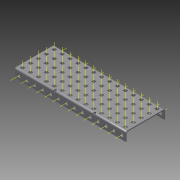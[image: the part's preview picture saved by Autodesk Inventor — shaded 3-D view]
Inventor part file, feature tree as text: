
AUTODESK INVENTOR PART (.ipt)
format: ipt  version: 2015 (Build 190159000, 159)  size: 2,581,504 bytes
history: native  units: in
note: dims shown in document units (in); Inventor stores cm internally (conversion verified against a paired STEP export)
features: other x104, pattern_linear x2, sheet_metal_op x1, extrude x1, imported_body x1, sketch x1
ambient origin geometry x8: Origin, YZ Plane, XZ Plane, XY Plane, X Axis, Y Axis, Z Axis, Center Point
bodies: Body1 (feature_tree)
feature tree (110):
  sheet_metal_op  "Fold1"
  other  "C-Channel"
  extrude  "length cut"  Depth=0.5in
  other  "top axis"
  other  "front axis"
  other  "back axis"
  pattern_linear  "top axes"  Spacing1=0.5in  [1 undecoded]
  pattern_linear  "horiz axes"  Spacing1=0.0in  [1 undecoded]
  other  "right plane"
  imported_body  "Base1"
  sketch  "Sketch1"  dims[d1=0.0in d4=0.5in d5=1.9685in d7=0.5in d10=0.5in d11=0.0in d12=0.0in d13=0.0in d14=-7.0in d15=0.0in d16=0.0in]
  other  "Work Point1"
  other  "Work Axis6"
  other  "Work Axis11"
  other  "Work Axis16"
  other  "Work Axis21"
  other  "Work Point2"
  other  "Work Point3"
  other  "Work Axis36"
  other  "Work Axis37"
  other  "Work Axis38"
  other  "Work Axis39"
  other  "Work Axis40"
  other  "Work Axis41"
  other  "Work Axis60"
  other  "Work Axis61"
  other  "Work Axis62"
  other  "Work Axis63"
  other  "Work Axis64"
  other  "Work Axis65"
  other  "Work Axis84"
  other  "Work Axis85"
  other  "Work Axis86"
  other  "Work Axis87"
  other  "Work Axis88"
  other  "Work Axis89"
  other  "Work Axis108"
  other  "Work Axis109"
  other  "Work Axis110"
  other  "Work Axis111"
  other  "Work Axis112"
  other  "Work Axis113"
  other  "Work Axis132"
  other  "Work Axis133"
  other  "Work Axis134"
  other  "Work Axis135"
  other  "Work Axis136"
  other  "Work Axis137"
  other  "Work Axis156"
  other  "Work Axis157"
  other  "Work Axis158"
  other  "Work Axis159"
  other  "Work Axis160"
  other  "Work Axis161"
  other  "Work Axis180"
  other  "Work Axis181"
  other  "Work Axis182"
  other  "Work Axis183"
  other  "Work Axis184"
  other  "Work Axis185"
  other  "Work Axis204"
  other  "Work Axis205"
  other  "Work Axis206"
  other  "Work Axis232"
  other  "Work Axis233"
  other  "Work Axis234"
  other  "Work Axis260"
  other  "Work Axis261"
  other  "Work Axis262"
  other  "Work Axis288"
  other  "Work Axis289"
  other  "Work Axis290"
  other  "Work Axis316"
  other  "Work Axis317"
  other  "Work Axis318"
  other  "Work Axis344"
  other  "Work Axis345"
  other  "Work Axis346"
  other  "Work Axis372"
  other  "Work Axis373"
  other  "Work Axis374"
  other  "left plane"
  other  "Work Axis400"
  other  "Work Axis401"
  other  "Work Axis402"
  other  "Work Axis403"
  other  "Work Axis404"
  other  "Work Axis405"
  other  "Work Axis406"
  other  "Work Axis407"
  other  "Work Axis408"
  other  "Work Axis409"
  other  "Work Axis410"
  other  "Work Axis411"
  other  "Work Axis412"
  other  "Work Axis413"
  other  "Work Axis414"
  other  "Work Axis415"
  other  "Work Axis416"
  other  "Work Axis417"
  other  "Work Axis418"
  other  "Work Axis419"
  other  "Work Axis420"
  other  "Work Axis421"
  other  "Work Axis422"
  other  "Work Axis423"
  other  "Work Axis424"
  other  "Work Axis425"
  other  "Work Axis426"
  other  "Work Axis427"
note: 2 required parameter values undecoded (feature->parameter linkage not recoverable at this tier; creation-order binding heuristic only, values carry confidence <= 0.55)
